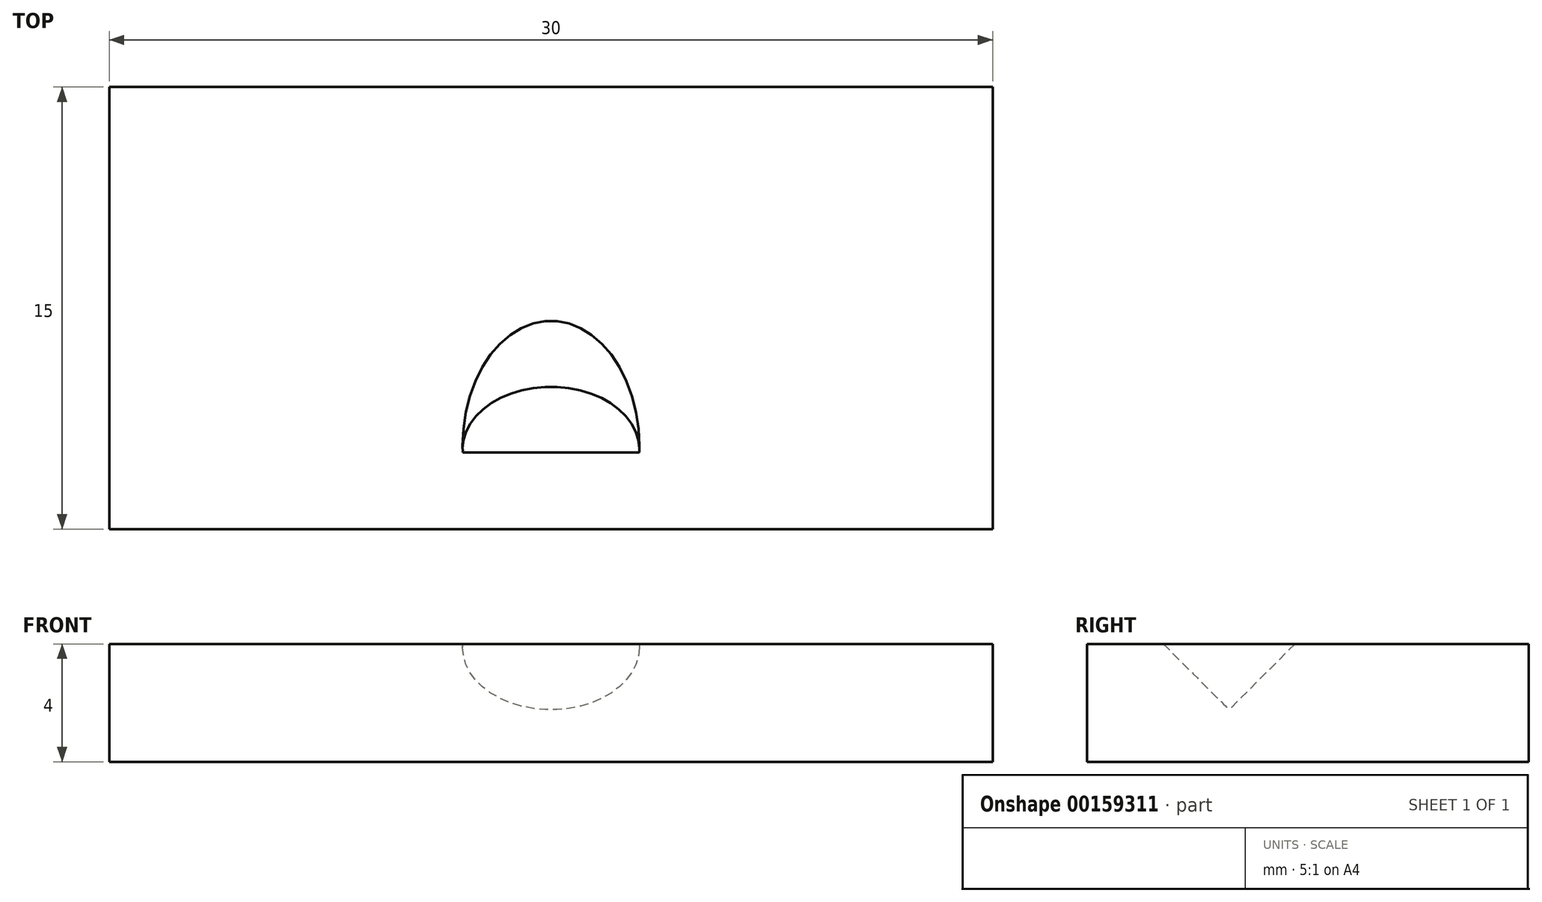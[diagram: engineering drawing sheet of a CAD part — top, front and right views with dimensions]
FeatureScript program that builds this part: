
annotation { "Feature Type Name" : "Feature", "Feature Type Description" : "" }
export const myFeature = defineFeature(function(context is Context, id is Id, definition is map)
    precondition{}
    {
        {
            var Q0;
            Q0=qCreatedBy(makeId("Top.planeOp"),FACE);
            var sketch = newSketch(context, id + "F0", { "sketchPlane" : qUnion([Q0])});
            skLineSegment(sketch, "E0.bottom", {"start": v(15, 7.5) * mm, "end": v(-15, 7.5) * mm});
            skLineSegment(sketch, "E0.top", {"start": v(15, -7.5) * mm, "end": v(-15, -7.5) * mm});
            skLineSegment(sketch, "E0.left", {"start": v(15, 7.5) * mm, "end": v(15, -7.5) * mm});
            skLineSegment(sketch, "E0.right", {"start": v(-15, 7.5) * mm, "end": v(-15, -7.5) * mm});
            skPoint(sketch, "E0.middle", {"position": v(0, 0) * mm});
            skSolve(sketch);
        }
        {
            var Q0;
            Q0 = qSketchRegion(id + "F0", true);
            extrude(context, id + "F1", {"entities" : qUnion([Q0]), "depth" : 4 * mm});
        }
        {
            var Q0;
            Q0=qCreatedBy(makeId("Top.planeOp"),FACE);
            var sketch = newSketch(context, id + "F2", { "sketchPlane" : qUnion([Q0])});
            skCircle(sketch, "E1", {"center": v(0, -2.5) * mm, "radius": 3 * mm});
            skSolve(sketch);
        }
        {
            var Q0;
            Q0 = qSketchRegion(id + "F2", true);
            extrude(context, id + "F3", {"entities" : qUnion([Q0]), "depth" : 25 * mm});
        }
        {
            var Q0;
            Q0=makeQuery(id+"F3.opExtrude","SWEPT_BODY",BODY,{"disambiguationData":[OSD([sQuery(id+"F2.wireOp",EDGE,"E1")])]});
            var Q1;
            Q1=makeQuery(id+"F1.opExtrude","CAP_EDGE",EDGE,{"disambiguationData":[OSD([sQuery(id+"F0.wireOp",EDGE,"E0.top")])],"isStart":false});
            transform(context, id + "F4", {"entities" : qUnion([Q0]), "transformType" : TransformType.ROTATION, "transformAxis" : qUnion([Q1]), "angle" : 45 * degree, "makeCopy" : false});
        }
        {
            var Q0;
            Q0=makeQuery(id+"F3.opExtrude","SWEPT_BODY",BODY,{"disambiguationData":[OSD([sQuery(id+"F2.wireOp",EDGE,"E1")])]});
            var Q1;
            Q1=makeQuery(id+"F1.opExtrude","CAP_EDGE",EDGE,{"disambiguationData":[OSD([sQuery(id+"F0.wireOp",EDGE,"E0.top")])],"isStart":true});
            transform(context, id + "F5", {"entities" : qUnion([Q0]), "transformType" : TransformType.TRANSLATION_3D, "dx" : 0 * mm, "dy" : 2 * mm, "dz" : 6.25 * mm, "makeCopy" : false});
        }
        {
            var Q0;
            Q0=makeQuery(id+"F3.opExtrude","SWEPT_BODY",BODY,{"disambiguationData":[OSD([sQuery(id+"F2.wireOp",EDGE,"E1")])]});
            var Q1;
            Q1=makeQuery(id+"F1.opExtrude","SWEPT_BODY",BODY,{"disambiguationData":[OSD([sQuery(id+"F0.wireOp",EDGE,"E0.bottom"),sQuery(id+"F0.wireOp",EDGE,"E0.top"),sQuery(id+"F0.wireOp",EDGE,"E0.left"),sQuery(id+"F0.wireOp",EDGE,"E0.right")])]});
            booleanBodies(context, id + "F6", {"operationType" : BooleanOperationType.SUBTRACTION, "tools" : qUnion([Q0]), "targets" : qUnion([Q1])});
        }
    });
